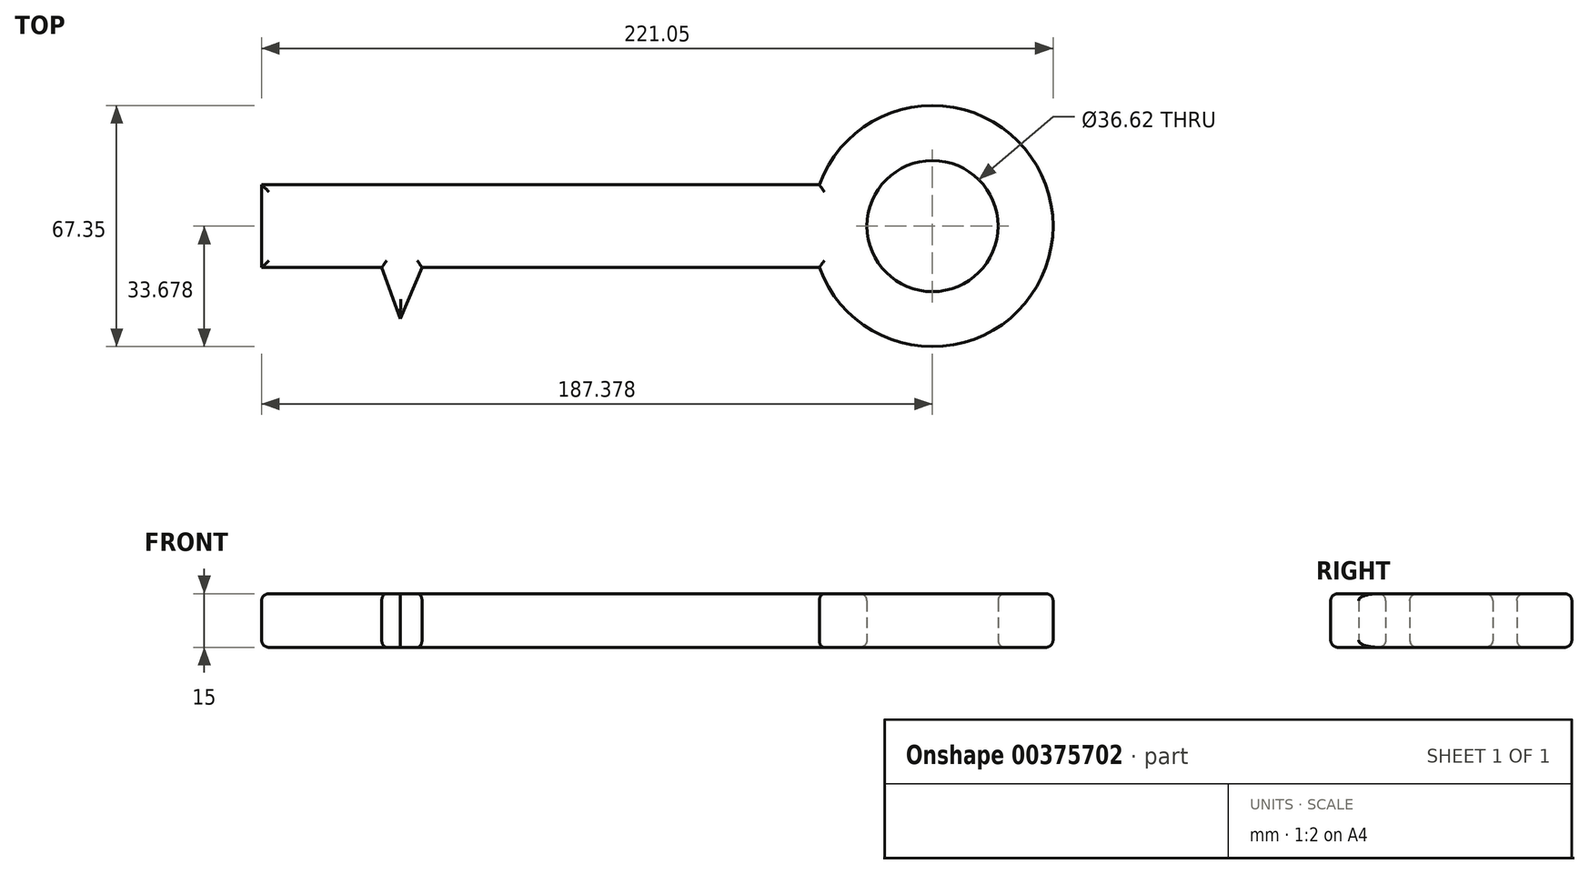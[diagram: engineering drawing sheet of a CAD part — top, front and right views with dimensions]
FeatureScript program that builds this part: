
annotation { "Feature Type Name" : "Feature", "Feature Type Description" : "" }
export const myFeature = defineFeature(function(context is Context, id is Id, definition is map)
    precondition{}
    {
        {
            var Q0;
            Q0=qCreatedBy(makeId("Top.planeOp"),FACE);
            var sketch = newSketch(context, id + "F0", { "sketchPlane" : qUnion([Q0])});
            skLineSegment(sketch, "E0.bottom", {"start": v(34.14, 34.3) * mm, "end": v(-121.62, 34.3) * mm});
            skLineSegment(sketch, "E0.top", {"start": v(34.14, 11.13) * mm, "end": v(-121.62, 11.13) * mm});
            skLineSegment(sketch, "E0.left", {"start": v(34.14, 34.3) * mm, "end": v(34.14, 11.13) * mm});
            skLineSegment(sketch, "E0.right", {"start": v(-121.62, 34.3) * mm, "end": v(-121.62, 11.13) * mm});
            skLineSegment(sketch, "E1.bottom", {"start": v(-121.62, 11.13) * mm, "end": v(-111.25, 11.13) * mm});
            skLineSegment(sketch, "E1.top", {"start": v(-121.62, -19.35) * mm, "end": v(-111.25, -19.35) * mm});
            skLineSegment(sketch, "E1.left", {"start": v(-121.62, 11.13) * mm, "end": v(-121.62, -19.35) * mm});
            skLineSegment(sketch, "E1.right", {"start": v(-111.25, 11.13) * mm, "end": v(-111.25, -19.35) * mm});
            skLineSegment(sketch, "E2.bottom", {"start": v(-103.94, 11.13) * mm, "end": v(-96.62, 11.13) * mm});
            skLineSegment(sketch, "E2.top", {"start": v(-103.94, -4.42) * mm, "end": v(-96.62, -4.42) * mm});
            skLineSegment(sketch, "E2.left", {"start": v(-103.94, 11.13) * mm, "end": v(-103.94, -4.42) * mm});
            skLineSegment(sketch, "E2.right", {"start": v(-96.62, 11.13) * mm, "end": v(-96.62, -4.42) * mm});
            skLineSegment(sketch, "E3", {"start": v(-88.09, 11.13) * mm, "end": v(-82.9, -3.2) * mm});
            skLineSegment(sketch, "E4", {"start": v(-82.9, -3.2) * mm, "end": v(-76.8, 11.13) * mm});
            skArc(sketch, "E5", {"start": v(34.14, 11.13) * mm, "mid": v(99.43, 22.7) * mm, "end": v(34.14, 34.3) * mm});
            skCircle(sketch, "E6", {"center": v(65.76, 22.7) * mm, "radius": 18.3 * mm});
            skSolve(sketch);
        }
        {
            var Q0;
            Q0=makeQuery(id+"F0.imprint","IMPRINT",FACE,{"disambiguationData":[TD([[makeQuery(id+"F0.imprint","IMPRINT",EDGE,{"derivedFrom":sQuery(id+"F0.wireOp",EDGE,"E0.bottom")}),1.0]])]});
            var Q1;
            {var subQ0=sQuery(id+"F0.wireOp",EDGE,"E3");Q1=makeQuery(id+"F0.imprint","IMPRINT",FACE,{"disambiguationData":[TD([[makeQuery(id+"F0.imprint","IMPRINT",EDGE,{"derivedFrom":subQ0}),1.0]])]});}
            var Q2;
            Q2=makeQuery(id+"F0.imprint","IMPRINT",FACE,{"disambiguationData":[TD([[makeQuery(id+"F0.imprint","IMPRINT",EDGE,{"derivedFrom":sQuery(id+"F0.wireOp",EDGE,"E2.bottom")}),-1.0]])]});
            var Q3;
            Q3=makeQuery(id+"F0.imprint","IMPRINT",FACE,{"disambiguationData":[TD([[makeQuery(id+"F0.imprint","IMPRINT",EDGE,{"derivedFrom":sQuery(id+"F0.wireOp",EDGE,"E1.bottom")}),-1.0]])]});
            var Q4;
            Q4=makeQuery(id+"F0.imprint","IMPRINT",FACE,{"disambiguationData":[TD([[makeQuery(id+"F0.imprint","IMPRINT",EDGE,{"derivedFrom":sQuery(id+"F0.wireOp",EDGE,"E0.left")}),1.0]])]});
            extrude(context, id + "F1", {"entities" : qUnion([Q0, Q1, Q2, Q3, Q4]), "depth" : 15 * mm});
        }
        {
            var Q0;
            Q0=makeQuery(id+"F1.opExtrude","CAP_FACE",FACE,{"disambiguationData":[OSD([sQuery(id+"F0.wireOp",EDGE,"E0.bottom"),sQuery(id+"F0.wireOp",EDGE,"E0.top"),sQuery(id+"F0.wireOp",EDGE,"E0.right"),sQuery(id+"F0.wireOp",EDGE,"E1.top"),sQuery(id+"F0.wireOp",EDGE,"E1.left"),sQuery(id+"F0.wireOp",EDGE,"E1.right"),sQuery(id+"F0.wireOp",EDGE,"E2.top"),sQuery(id+"F0.wireOp",EDGE,"E2.left"),sQuery(id+"F0.wireOp",EDGE,"E2.right"),sQuery(id+"F0.wireOp",EDGE,"E3"),sQuery(id+"F0.wireOp",EDGE,"E4"),sQuery(id+"F0.wireOp",EDGE,"E5"),sQuery(id+"F0.wireOp",EDGE,"E6")])],"isStart":true});
            var Q1;
            Q1=makeQuery(id+"F1.opExtrude","CAP_FACE",FACE,{"disambiguationData":[OSD([sQuery(id+"F0.wireOp",EDGE,"E0.bottom"),sQuery(id+"F0.wireOp",EDGE,"E0.top"),sQuery(id+"F0.wireOp",EDGE,"E0.right"),sQuery(id+"F0.wireOp",EDGE,"E1.top"),sQuery(id+"F0.wireOp",EDGE,"E1.left"),sQuery(id+"F0.wireOp",EDGE,"E1.right"),sQuery(id+"F0.wireOp",EDGE,"E2.top"),sQuery(id+"F0.wireOp",EDGE,"E2.left"),sQuery(id+"F0.wireOp",EDGE,"E2.right"),sQuery(id+"F0.wireOp",EDGE,"E3"),sQuery(id+"F0.wireOp",EDGE,"E4"),sQuery(id+"F0.wireOp",EDGE,"E5"),sQuery(id+"F0.wireOp",EDGE,"E6")])],"isStart":false});
            fillet(context, id + "F2", {"entities" : qUnion([Q0, Q1]), "radius" : 2 * mm, "tangentPropagation" : true, "allowEdgeOverflow" : false});
        }
    });
